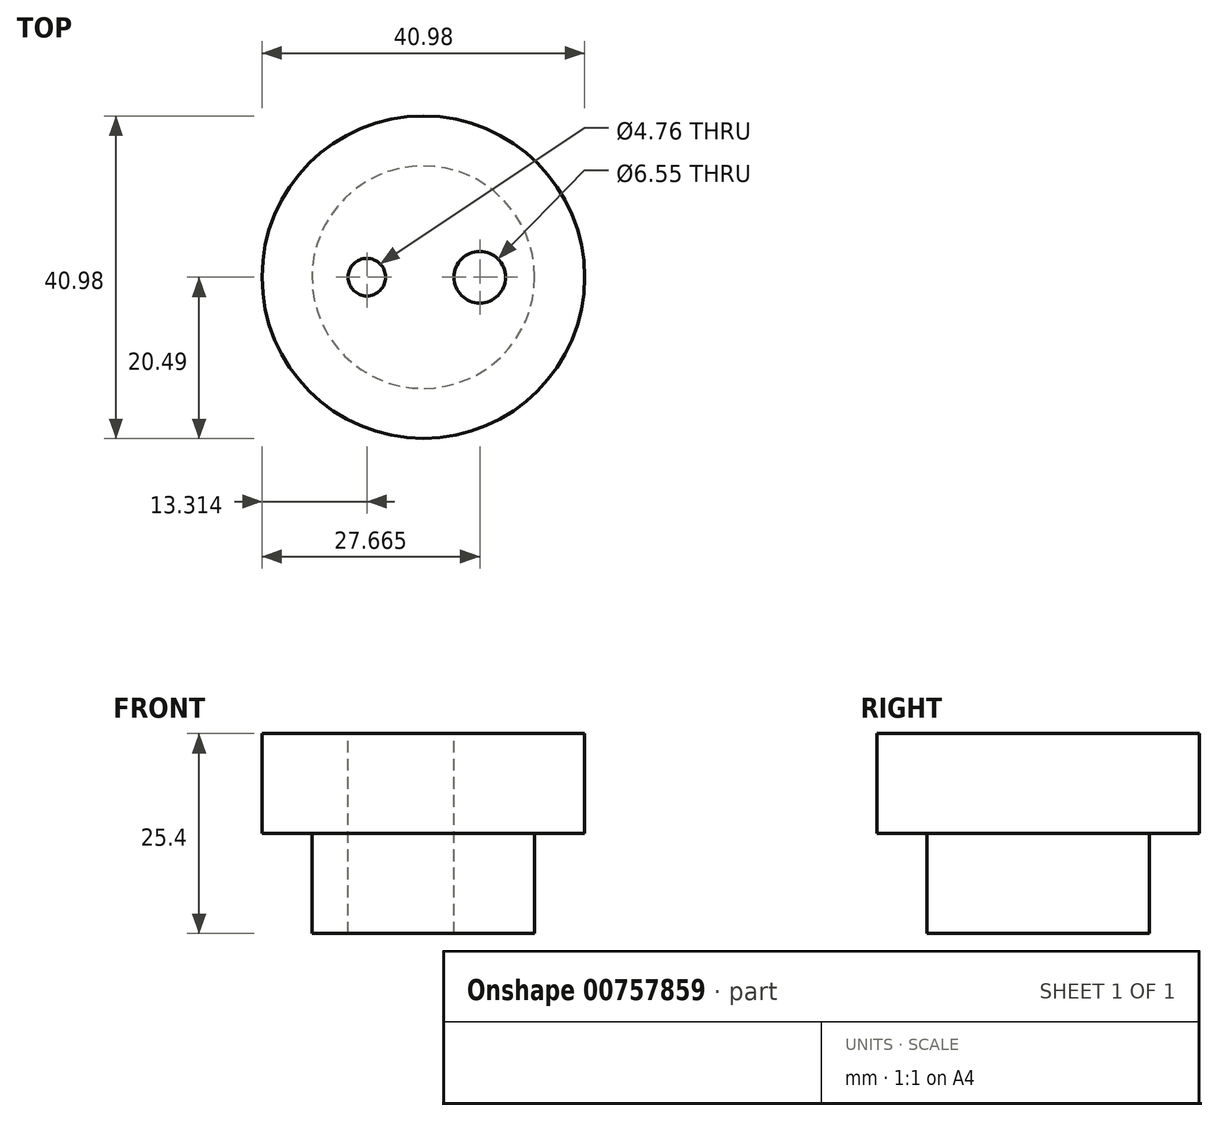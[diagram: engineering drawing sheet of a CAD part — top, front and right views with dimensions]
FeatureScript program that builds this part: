
annotation { "Feature Type Name" : "Feature", "Feature Type Description" : "" }
export const myFeature = defineFeature(function(context is Context, id is Id, definition is map)
    precondition{}
    {
        {
            var Q0;
            Q0=qCreatedBy(makeId("Front.planeOp"),FACE);
            var sketch = newSketch(context, id + "F0", { "sketchPlane" : qUnion([Q0])});
            skLineSegment(sketch, "E0.bottom", {"start": v(0, -12.7) * mm, "end": v(14.14, -12.7) * mm});
            skLineSegment(sketch, "E0.top", {"start": v(0, 12.7) * mm, "end": v(20.49, 12.7) * mm});
            skLineSegment(sketch, "E0.left", {"start": v(0, -12.7) * mm, "end": v(0, 12.7) * mm});
            skLineSegment(sketch, "E0.right", {"start": v(20.49, 0) * mm, "end": v(20.49, 12.7) * mm});
            skLineSegment(sketch, "E1", {"start": v(14.14, 0) * mm, "end": v(20.49, 0) * mm});
            skLineSegment(sketch, "E2", {"start": v(14.14, 0) * mm, "end": v(14.14, -12.7) * mm});
            skPoint(sketch, "E3.orphan", {"position": v(20.49, -12.7) * mm});
            skSolve(sketch);
        }
        {
            var Q0;
            Q0 = qSketchRegion(id + "F0", true);
            var Q1;
            Q1=sQuery(id+"F0.wireOp",EDGE,"E0.left");
            revolve(context, id + "F1", {"surfaceOperationType" : NewSurfaceOperationType.NEW, "entities" : qUnion([Q0]), "axis" : qUnion([Q1]), "revolveType" : RevolveType.FULL});
        }
        {
            var Q0;
            Q0=qCreatedBy(makeId("Top.planeOp"),FACE);
            var sketch = newSketch(context, id + "F2", { "sketchPlane" : qUnion([Q0])});
            skCircle(sketch, "E4", {"center": v(7.18, 0) * mm, "radius": 3.28 * mm});
            skCircle(sketch, "E5", {"center": v(-7.18, 0) * mm, "radius": 2.38 * mm});
            skSolve(sketch);
        }
        {
            var Q0;
            Q0 = qSketchRegion(id + "F2", true);
            extrude(context, id + "F3", {"entities" : qUnion([Q0]), "operationType" : NewBodyOperationType.REMOVE, "endBound" : BoundingType.THROUGH_ALL, "oppositeDirection" : true, "depth" : 25.4 * mm, "offsetDistance" : 25.4 * mm, "hasSecondDirection" : true, "secondDirectionBound" : SecondDirectionBoundingType.THROUGH_ALL, "secondDirectionOppositeDirection" : false, "secondDirectionDepth" : 25.4 * mm});
        }
    });
